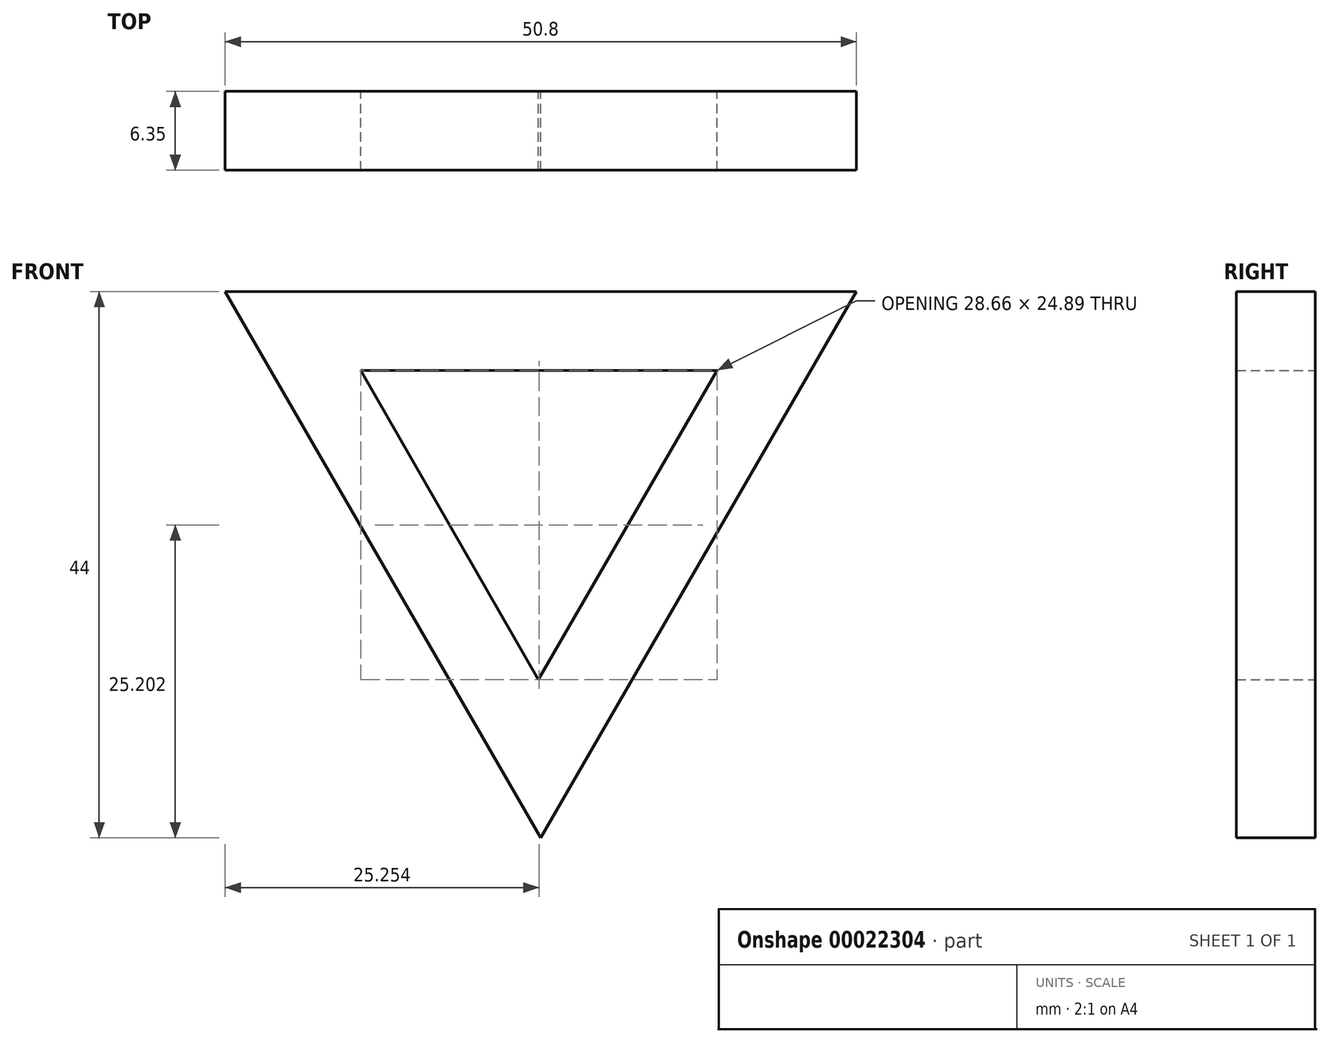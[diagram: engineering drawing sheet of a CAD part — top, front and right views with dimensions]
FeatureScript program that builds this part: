
annotation { "Feature Type Name" : "Feature", "Feature Type Description" : "" }
export const myFeature = defineFeature(function(context is Context, id is Id, definition is map)
    precondition{}
    {
        {
            var Q0;
            Q0=qCreatedBy(makeId("Front.planeOp"),FACE);
            var sketch = newSketch(context, id + "F0", { "sketchPlane" : qUnion([Q0])});
            skLineSegment(sketch, "E0", {"start": v(-25.4, 24.66) * mm, "end": v(25.4, 24.66) * mm});
            skLineSegment(sketch, "E1", {"start": v(-25.4, 24.66) * mm, "end": v(0, -19.34) * mm});
            skLineSegment(sketch, "E2", {"start": v(0, -19.34) * mm, "end": v(25.4, 24.66) * mm});
            skLineSegment(sketch, "E3", {"start": v(-14.48, 18.3) * mm, "end": v(14.19, 18.3) * mm});
            skLineSegment(sketch, "E4.trimOffspring", {"start": v(14.19, 18.3) * mm, "end": v(-0.19, -6.58) * mm});
            skLineSegment(sketch, "E5.trimOffspring", {"start": v(-0.19, -6.58) * mm, "end": v(-14.48, 18.3) * mm});
            skSolve(sketch);
        }
        {
            var Q0;
            Q0 = qSketchRegion(id + "F0", true);
            extrude(context, id + "F1", {"entities" : qUnion([Q0]), "depth" : 6.35 * mm});
        }
    });
